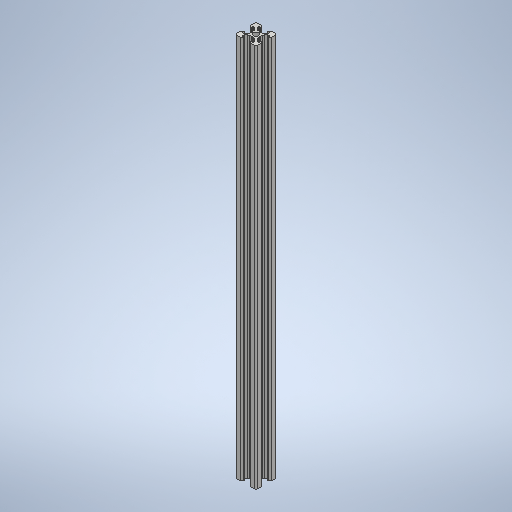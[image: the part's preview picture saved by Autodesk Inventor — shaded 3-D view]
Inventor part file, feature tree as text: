
AUTODESK INVENTOR PART (.ipt)
format: ipt  version: 2025.2 (Build 292293000, 293)  size: 403,968 bytes
history: native  units: mm
features: other x1, extrude x1, sketch x1
ambient origin geometry x8: Origin, YZ Plane, XZ Plane, XY Plane, X Axis, Y Axis, Z Axis, Center Point
bodies: Body1 (feature_tree)
feature tree (3):
  other  "Твердое тело1"
  extrude  "Выдавливание1"  Depth=0.25mm
  sketch  "Эскиз1"
